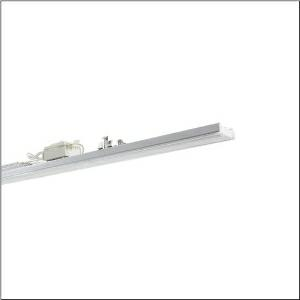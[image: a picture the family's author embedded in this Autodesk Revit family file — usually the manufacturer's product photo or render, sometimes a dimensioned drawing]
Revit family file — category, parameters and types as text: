
# Revit family: licross_21_recessed_ho_52tl12dn4fxm3s4
name_source: partatom
category: Lighting Fixtures
units: mm (PartAtom-declared; Revit-internal decimal feet)

## family parameters
Cut with Voids When Loaded = No
Host = Face
Light Source = No
Part Type = Normal
Room Calculation Point = No
Round Connector Dimension = Use Diameter
Shared = No

## types (1)
- --- (1 x LED, 930 lm, 7.5 W, 4000K)
    Apparent Load = 8 VA
    CIE Flux Codes = 69 91 98 100 100
    Color Rendering = 80
    Color Temperature = 4000K
    Default Elevation = 1800 mm
    Description = Licross 21 Recessed HO, luminaire insert, of sheet steel, galvanised, coil coated, white, length: 1.500mm, width: 66mm, height: 67mm, LED rated luminous flux: 15.000lm, light colour: 840, SDCM (Standard Deviation of Colour Matching)MacAdam ≤ 3 SDCM (initial), control gear: DALI 2, with plug, 6-pole, with phase selection, for trunking rail, 9 or 11-core, mains connection: 220..240V, AC, 50/60Hz, rated input power: 88W, internal wiring halogen-free, for emergency light function, for trunking rail, 9-/11-core, converter,control gear: single battery element, battery: LiFePO4, 9Ah, primary optical cover: cover, of PMMA, light emission: direct distribution, primary light characteristic: symmetric, protection rating (complete): IP40, insulation class (complete): insulation class I (protective earthing), certification: CE, UKCA, protection symbol: D if used in an environment without relevant dust loads with corresponding accessories, impact resistance: IK06, permissible ambient temperature for indoor applications: +5..+35°C, standard: EN 60598-2-22, LABS conformity tested according to VDMA 24364:2018-05, reducing of maximum allowable ambient temperature of 5°C with ceiling mounting, corresponds to IFS (International Featured Standards) requirements for safety and quality in the food industry, The light source and the operating device comply with the requirements of the Ecodesign Regulation (EU) 2019/2020 and are replaceable in accordance with this regulation, packaging unit: 1 piece
    Height = 58 mm
    Lamp = 1 x LED
    Lamp Light Flux = 930 lm
    Lamp Power = 7.5 W
    Lamp count = 1
    Length = 1500 mm
    Luminous efficacy = 124 lm/W
    Manufacturer = Siteco
    ModVariant = No
    Model = 52TL12DN4FXM3S4
    Mounting Place = Ceiling
    Mounting Type = Pendant
    Number of Poles = 1
    OnlyDefault = Yes
    Power Factor = 1
    Product Name = Licross 21 Recessed HO
    Product group = luminaire insert | ceiling pendant
    ProductGroupID = 901
    Protection Class = Protection class I
    Protection Degree = IP 40
    RLX_Detail_Level = 1
    RLX_Emergency_Light_Flux = 0 lm
    RLX_Emergency_Type = 0
    RLX_Emergency_Type_DB = No
    RlxData = <blob elided: 25405 chars, md5=2d5abe3c>
    Socket = socket
    Standby Power = 0 W
    System Light Flux = 930 lm
    System Power = 8 W
    Type Comments = : emergency light operation: 3 h
    Type Image = l_1296930.jpg
    URL = http://relux.com
    VarID = @adj_109219
    Voltage = 0 V
    Weight = 0.00 kg
    Width = 66 mm

## geometry (parser evidence)
native form markers: Blend x4, Sweep x11
no freeform markers — native parametric forms only
